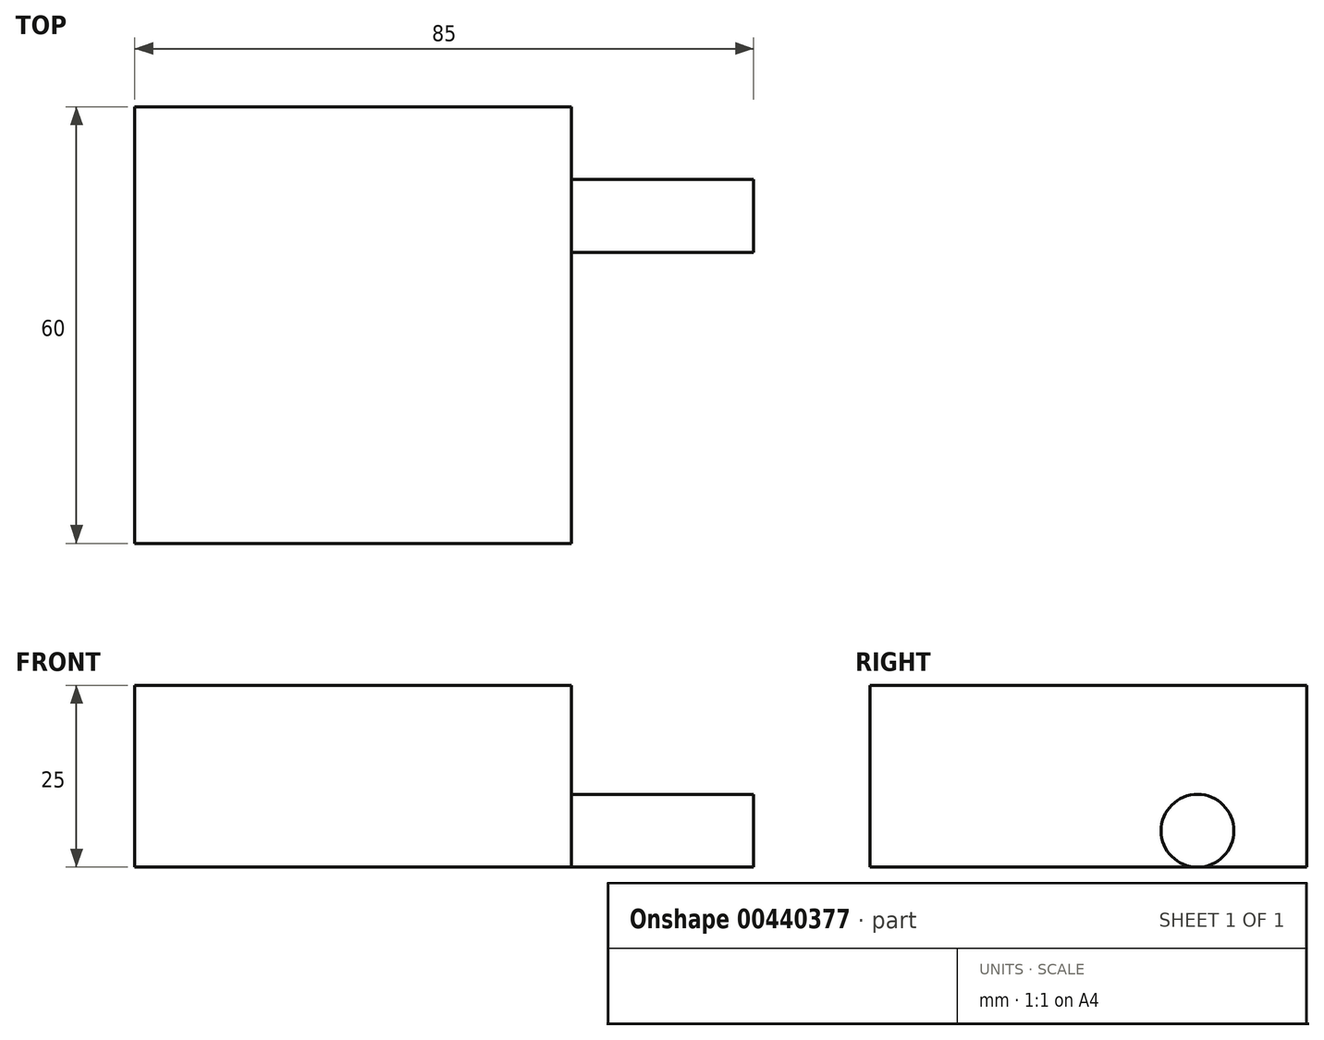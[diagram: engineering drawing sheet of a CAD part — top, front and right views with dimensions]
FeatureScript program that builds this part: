
annotation { "Feature Type Name" : "Feature", "Feature Type Description" : "" }
export const myFeature = defineFeature(function(context is Context, id is Id, definition is map)
    precondition{}
    {
        {
            var Q0;
            Q0=qCreatedBy(makeId("Top.planeOp"),FACE);
            var sketch = newSketch(context, id + "F0", { "sketchPlane" : qUnion([Q0])});
            skLineSegment(sketch, "E0.bottom", {"start": v(30, -30) * mm, "end": v(-30, -30) * mm});
            skLineSegment(sketch, "E0.top", {"start": v(30, 30) * mm, "end": v(-30, 30) * mm});
            skLineSegment(sketch, "E0.left", {"start": v(30, -30) * mm, "end": v(30, 30) * mm});
            skLineSegment(sketch, "E0.right", {"start": v(-30, -30) * mm, "end": v(-30, 30) * mm});
            skPoint(sketch, "E0.middle", {"position": v(0, 0) * mm});
            skSolve(sketch);
        }
        {
            var Q0;
            Q0 = qSketchRegion(id + "F0", true);
            extrude(context, id + "F1", {"entities" : qUnion([Q0]), "depth" : 25 * mm});
        }
        {
            var Q0;
            Q0=makeQuery(id+"F1.opExtrude","SWEPT_FACE",FACE,{"disambiguationData":[OSD([sQuery(id+"F0.wireOp",EDGE,"E0.left")])]});
            var sketch = newSketch(context, id + "F2", { "sketchPlane" : qUnion([Q0])});
            skCircle(sketch, "E1", {"center": v(15, 5) * mm, "radius": 5 * mm});
            skSolve(sketch);
        }
        {
            var Q0;
            Q0 = qSketchRegion(id + "F2", true);
            extrude(context, id + "F3", {"entities" : qUnion([Q0]), "operationType" : NewBodyOperationType.ADD, "depth" : 25 * mm});
        }
    });
